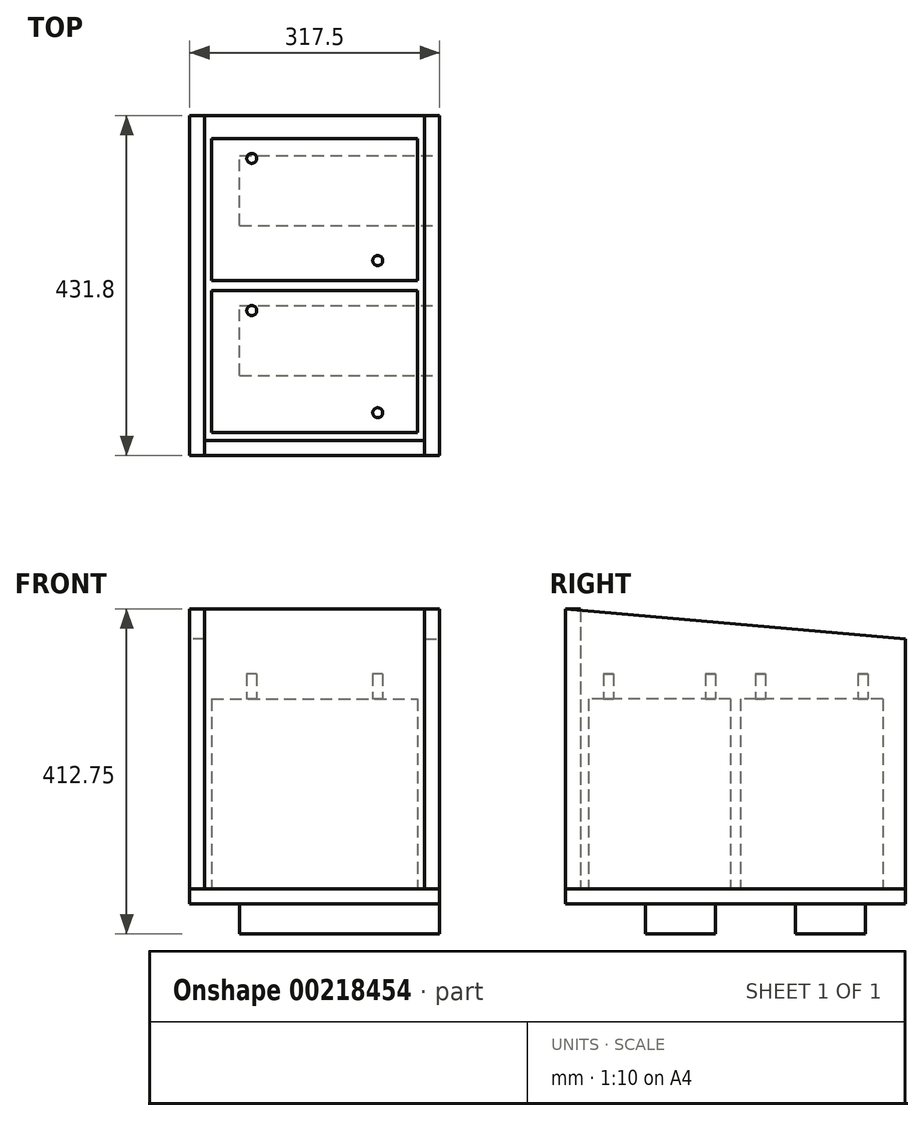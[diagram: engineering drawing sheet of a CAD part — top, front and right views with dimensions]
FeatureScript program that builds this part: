
annotation { "Feature Type Name" : "Feature", "Feature Type Description" : "" }
export const myFeature = defineFeature(function(context is Context, id is Id, definition is map)
    precondition{}
    {
        {
            var Q0;
            Q0=qCreatedBy(makeId("Top.planeOp"),FACE);
            var sketch = newSketch(context, id + "F0", { "sketchPlane" : qUnion([Q0])});
            skLineSegment(sketch, "E0.bottom", {"start": v(0, 0) * mm, "end": v(-260.35, 0) * mm});
            skLineSegment(sketch, "E0.top", {"start": v(0, 469.9) * mm, "end": v(-260.35, 469.9) * mm});
            skLineSegment(sketch, "E0.left", {"start": v(0, 0) * mm, "end": v(0, 469.9) * mm});
            skLineSegment(sketch, "E0.right", {"start": v(-260.35, 0) * mm, "end": v(-260.35, 469.9) * mm});
            skSolve(sketch);
        }
        {
            var Q0;
            Q0=qCreatedBy(makeId("Right.planeOp"),FACE);
            var sketch = newSketch(context, id + "F1", { "sketchPlane" : qUnion([Q0])});
            skLineSegment(sketch, "E1.bottom", {"start": v(0, 0) * mm, "end": v(469.9, 0) * mm});
            skLineSegment(sketch, "E1.top", {"start": v(0, 774.7) * mm, "end": v(469.9, 774.7) * mm});
            skLineSegment(sketch, "E1.left", {"start": v(0, 0) * mm, "end": v(0, 774.7) * mm});
            skLineSegment(sketch, "E1.right", {"start": v(469.9, 0) * mm, "end": v(469.9, 774.7) * mm});
            skSolve(sketch);
        }
        {
            var Q0;
            Q0=makeQuery(id+"F1.imprint","IMPRINT",FACE,{"disambiguationData":[TD([[makeQuery(id+"F1.imprint","IMPRINT",EDGE,{"derivedFrom":sQuery(id+"F1.wireOp",EDGE,"E1.bottom")}),1.0]])]});
            var sketch = newSketch(context, id + "F2", { "sketchPlane" : qUnion([Q0])});
            skLineSegment(sketch, "E2.bottom", {"start": v(101.6, 0) * mm, "end": v(190.5, 0) * mm});
            skLineSegment(sketch, "E2.top", {"start": v(101.6, 38.1) * mm, "end": v(190.5, 38.1) * mm});
            skLineSegment(sketch, "E2.left", {"start": v(101.6, 0) * mm, "end": v(101.6, 38.1) * mm});
            skLineSegment(sketch, "E2.right", {"start": v(190.5, 0) * mm, "end": v(190.5, 38.1) * mm});
            skLineSegment(sketch, "E3.bottom", {"start": v(292.1, 0) * mm, "end": v(381, 0) * mm});
            skLineSegment(sketch, "E3.top", {"start": v(292.1, 38.1) * mm, "end": v(381, 38.1) * mm});
            skLineSegment(sketch, "E3.left", {"start": v(292.1, 0) * mm, "end": v(292.1, 38.1) * mm});
            skLineSegment(sketch, "E3.right", {"start": v(381, 0) * mm, "end": v(381, 38.1) * mm});
            skSolve(sketch);
        }
        {
            var Q0;
            Q0 = qSketchRegion(id + "F2", true);
            extrude(context, id + "F3", {"entities" : qUnion([Q0]), "oppositeDirection" : true, "depth" : 254 * mm});
        }
        {
            var Q0;
            Q0=makeQuery(id+"F3.opExtrude","SWEPT_FACE",FACE,{"disambiguationData":[OSD([sQuery(id+"F2.wireOp",EDGE,"E2.top")])]});
            var sketch = newSketch(context, id + "F4", { "sketchPlane" : qUnion([Q0])});
            skLineSegment(sketch, "E4.bottom", {"start": v(0, 431.8) * mm, "end": v(-317.5, 431.8) * mm});
            skLineSegment(sketch, "E4.top", {"start": v(0, 0) * mm, "end": v(-317.5, 0) * mm});
            skLineSegment(sketch, "E4.left", {"start": v(0, 431.8) * mm, "end": v(0, 0) * mm});
            skLineSegment(sketch, "E4.right", {"start": v(-317.5, 431.8) * mm, "end": v(-317.5, 0) * mm});
            skSolve(sketch);
        }
        {
            var Q0;
            Q0 = qSketchRegion(id + "F4", true);
            extrude(context, id + "F5", {"entities" : qUnion([Q0]), "depth" : 19.05 * mm});
        }
        {
            var Q0;
            Q0=makeQuery(id+"F5.opExtrude","SWEPT_FACE",FACE,{"disambiguationData":[OSD([sQuery(id+"F4.wireOp",EDGE,"E4.right")])]});
            var sketch = newSketch(context, id + "F6", { "sketchPlane" : qUnion([Q0])});
            skLineSegment(sketch, "E5", {"start": v(-431.8, 57.15) * mm, "end": v(0, 57.15) * mm});
            skLineSegment(sketch, "E6", {"start": v(0, 57.15) * mm, "end": v(0, 412.75) * mm});
            skLineSegment(sketch, "E7", {"start": v(0, 412.75) * mm, "end": v(-431.8, 374.65) * mm});
            skLineSegment(sketch, "E8", {"start": v(-431.8, 374.65) * mm, "end": v(-431.8, 57.15) * mm});
            skSolve(sketch);
        }
        {
            var Q0;
            Q0 = qSketchRegion(id + "F6", true);
            extrude(context, id + "F7", {"entities" : qUnion([Q0]), "oppositeDirection" : true, "depth" : 19.05 * mm});
        }
        {
            var Q0;
            Q0=makeQuery(id+"F5.opExtrude","SWEPT_FACE",FACE,{"disambiguationData":[OSD([sQuery(id+"F4.wireOp",EDGE,"E4.left")])]});
            var sketch = newSketch(context, id + "F8", { "sketchPlane" : qUnion([Q0])});
            skLineSegment(sketch, "E9.0.0", {"start": v(431.8, 374.65) * mm, "end": v(0, 412.75) * mm});
            skLineSegment(sketch, "E9.0.1", {"start": v(0, 412.75) * mm, "end": v(0, 57.15) * mm});
            skLineSegment(sketch, "E9.0.2", {"start": v(0, 57.15) * mm, "end": v(431.8, 57.15) * mm});
            skLineSegment(sketch, "E9.0.3", {"start": v(431.8, 57.15) * mm, "end": v(431.8, 374.65) * mm});
            skSolve(sketch);
        }
        {
            var Q0;
            Q0 = qSketchRegion(id + "F8", true);
            extrude(context, id + "F9", {"entities" : qUnion([Q0]), "oppositeDirection" : true, "depth" : 19.05 * mm});
        }
        {
            var Q0;
            Q0=makeQuery(id+"F5.opExtrude","CAP_FACE",FACE,{"disambiguationData":[OSD([sQuery(id+"F4.wireOp",EDGE,"E4.bottom"),sQuery(id+"F4.wireOp",EDGE,"E4.top"),sQuery(id+"F4.wireOp",EDGE,"E4.left"),sQuery(id+"F4.wireOp",EDGE,"E4.right")])],"isStart":false});
            var sketch = newSketch(context, id + "F10", { "sketchPlane" : qUnion([Q0])});
            skLineSegment(sketch, "E10.bottom", {"start": v(-289.56, 402.84) * mm, "end": v(-27.94, 402.84) * mm});
            skLineSegment(sketch, "E10.top", {"start": v(-289.56, 222.25) * mm, "end": v(-27.94, 222.25) * mm});
            skLineSegment(sketch, "E10.left", {"start": v(-289.56, 402.84) * mm, "end": v(-289.56, 222.25) * mm});
            skLineSegment(sketch, "E10.right", {"start": v(-27.94, 402.84) * mm, "end": v(-27.94, 222.25) * mm});
            skLineSegment(sketch, "E11.bottom", {"start": v(-27.94, 209.55) * mm, "end": v(-289.56, 209.55) * mm});
            skLineSegment(sketch, "E11.top", {"start": v(-27.94, 28.96) * mm, "end": v(-289.56, 28.96) * mm});
            skLineSegment(sketch, "E11.left", {"start": v(-27.94, 209.55) * mm, "end": v(-27.94, 28.96) * mm});
            skLineSegment(sketch, "E11.right", {"start": v(-289.56, 209.55) * mm, "end": v(-289.56, 28.96) * mm});
            skLineSegment(sketch, "E12", {"start": v(-158.75, 28.96) * mm, "end": v(-158.75, 0) * mm, "construction": true});
            skLineSegment(sketch, "E13", {"start": v(-158.75, 402.84) * mm, "end": v(-158.75, 431.8) * mm, "construction": true});
            skLineSegment(sketch, "E14", {"start": v(-27.94, 119.25) * mm, "end": v(0, 119.25) * mm, "construction": true});
            skLineSegment(sketch, "E15", {"start": v(-289.56, 119.25) * mm, "end": v(-317.5, 119.25) * mm, "construction": true});
            skSolve(sketch);
        }
        {
            var Q0;
            Q0 = qSketchRegion(id + "F10", true);
            extrude(context, id + "F11", {"entities" : qUnion([Q0]), "depth" : 241.3 * mm});
        }
        {
            var Q0;
            Q0=makeQuery(id+"F11.opExtrude","CAP_FACE",FACE,{"disambiguationData":[OSD([sQuery(id+"F10.wireOp",EDGE,"E10.bottom"),sQuery(id+"F10.wireOp",EDGE,"E10.top"),sQuery(id+"F10.wireOp",EDGE,"E10.left"),sQuery(id+"F10.wireOp",EDGE,"E10.right")])],"isStart":false});
            var sketch = newSketch(context, id + "F12", { "sketchPlane" : qUnion([Q0])});
            skCircle(sketch, "E16", {"center": v(-238.76, 377.44) * mm, "radius": 6.35 * mm});
            skCircle(sketch, "E17", {"center": v(-78.74, 247.65) * mm, "radius": 6.35 * mm});
            skCircle(sketch, "E18", {"center": v(-238.76, 184.15) * mm, "radius": 6.35 * mm});
            skCircle(sketch, "E19", {"center": v(-78.74, 54.36) * mm, "radius": 6.35 * mm});
            skLineSegment(sketch, "E20", {"start": v(-238.76, 377.44) * mm, "end": v(-238.76, 402.84) * mm, "construction": true});
            skLineSegment(sketch, "E21", {"start": v(-238.76, 377.44) * mm, "end": v(-289.56, 377.44) * mm, "construction": true});
            skLineSegment(sketch, "E22", {"start": v(-78.74, 247.65) * mm, "end": v(-78.74, 222.25) * mm, "construction": true});
            skLineSegment(sketch, "E23", {"start": v(-78.74, 247.65) * mm, "end": v(-27.94, 247.65) * mm, "construction": true});
            skLineSegment(sketch, "E24", {"start": v(-78.74, 54.36) * mm, "end": v(-78.74, 28.96) * mm, "construction": true});
            skLineSegment(sketch, "E25", {"start": v(-238.76, 184.15) * mm, "end": v(-238.76, 209.55) * mm, "construction": true});
            skSolve(sketch);
        }
        {
            var Q0;
            Q0 = qSketchRegion(id + "F12", true);
            extrude(context, id + "F13", {"entities" : qUnion([Q0]), "operationType" : NewBodyOperationType.ADD, "depth" : 31.75 * mm});
        }
        {
            var Q0;
            Q0=makeQuery(id+"F5.opExtrude","CAP_FACE",FACE,{"disambiguationData":[OSD([sQuery(id+"F4.wireOp",EDGE,"E4.bottom"),sQuery(id+"F4.wireOp",EDGE,"E4.top"),sQuery(id+"F4.wireOp",EDGE,"E4.left"),sQuery(id+"F4.wireOp",EDGE,"E4.right")])],"isStart":false});
            var sketch = newSketch(context, id + "F14", { "sketchPlane" : qUnion([Q0])});
            skLineSegment(sketch, "E26.bottom", {"start": v(-298.45, 0) * mm, "end": v(-19.05, 0) * mm});
            skLineSegment(sketch, "E26.top", {"start": v(-298.45, 19.05) * mm, "end": v(-19.05, 19.05) * mm});
            skLineSegment(sketch, "E26.left", {"start": v(-298.45, 0) * mm, "end": v(-298.45, 19.05) * mm});
            skLineSegment(sketch, "E26.right", {"start": v(-19.05, 0) * mm, "end": v(-19.05, 19.05) * mm});
            skSolve(sketch);
        }
        {
            var Q0;
            Q0 = qSketchRegion(id + "F14", true);
            var Q1;
            Q1=makeQuery(id+"F7.opExtrude","CAP_VERTEX",VERTEX,{"disambiguationData":[OSD([sQuery(id+"F6.wireOp",EDGE,"E6"),sQuery(id+"F6.wireOp",EDGE,"E7")])],"isStart":false});
            extrude(context, id + "F15", {"entities" : qUnion([Q0]), "endBound" : BoundingType.UP_TO_VERTEX, "endBoundEntityVertex" : qUnion([Q1]), "depth" : 25.4 * mm});
        }
    });
